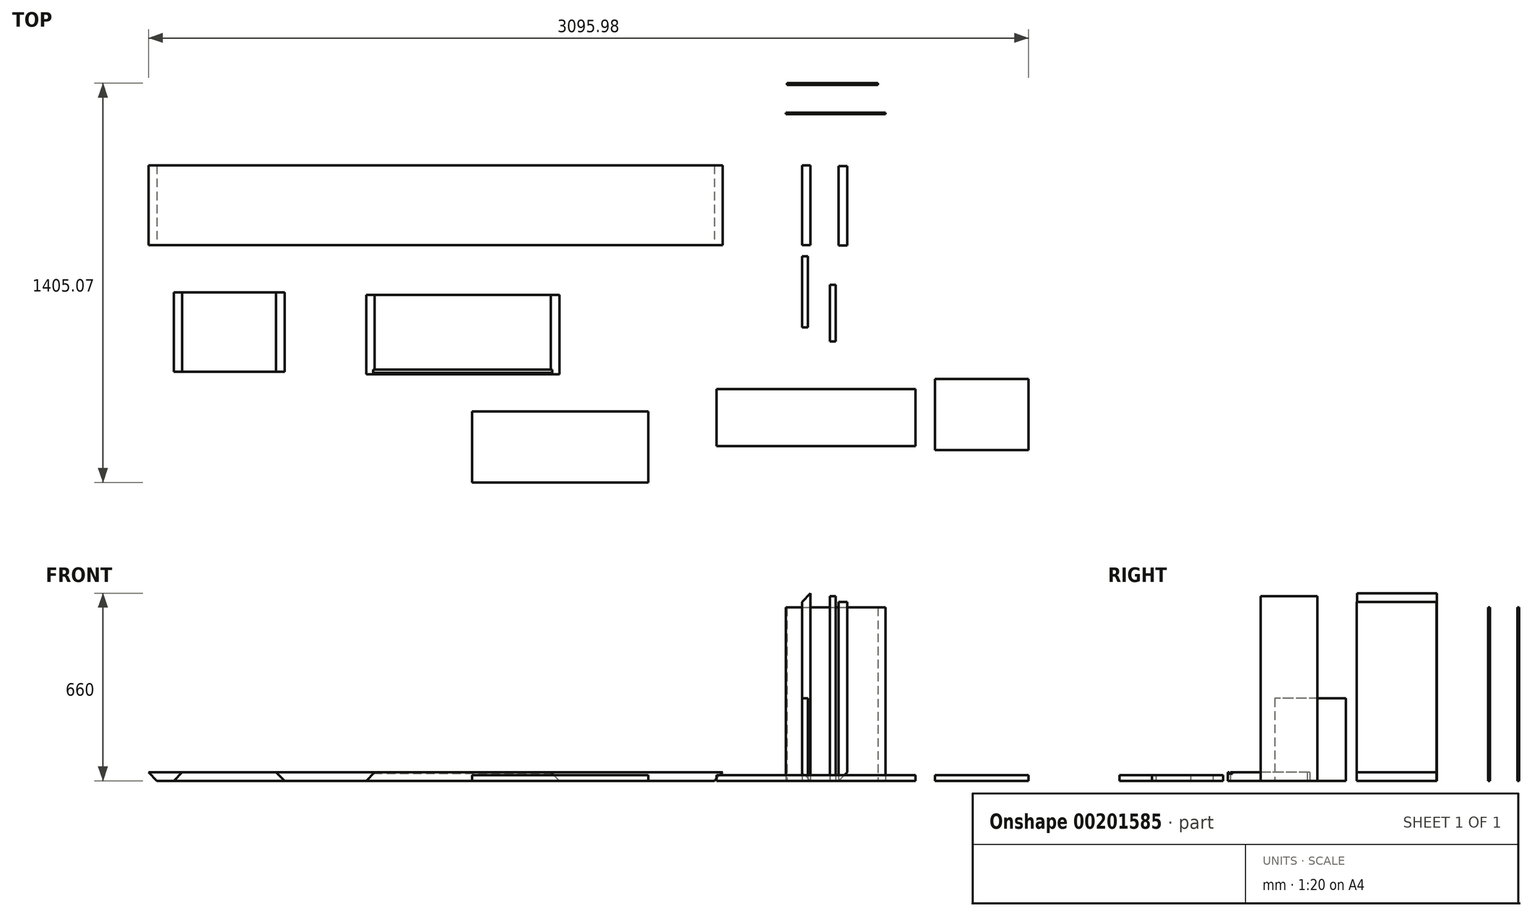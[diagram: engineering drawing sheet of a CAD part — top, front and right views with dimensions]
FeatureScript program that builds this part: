
annotation { "Feature Type Name" : "Feature", "Feature Type Description" : "" }
export const myFeature = defineFeature(function(context is Context, id is Id, definition is map)
    precondition{}
    {
        {
            var Q0;
            Q0=qCreatedBy(makeId("Top.planeOp"),FACE);
            var sketch = newSketch(context, id + "F0", { "sketchPlane" : qUnion([Q0])});
            skLineSegment(sketch, "E0.bottom", {"start": v(-100, 0) * mm, "end": v(-2120, 0) * mm});
            skLineSegment(sketch, "E0.top", {"start": v(-100, 280) * mm, "end": v(-2120, 280) * mm});
            skLineSegment(sketch, "E0.left", {"start": v(-100, 0) * mm, "end": v(-100, 280) * mm});
            skLineSegment(sketch, "E0.right", {"start": v(-2120, 0) * mm, "end": v(-2120, 280) * mm});
            skSolve(sketch);
        }
        {
            var Q0;
            Q0=makeQuery(id+"F0.imprint","IMPRINT",FACE,{"disambiguationData":[TD([[makeQuery(id+"F0.imprint","IMPRINT",EDGE,{"derivedFrom":sQuery(id+"F0.wireOp",EDGE,"E0.bottom")}),-1.0]])]});
            extrude(context, id + "F1", {"entities" : qUnion([Q0]), "depth" : 30 * mm});
        }
        {
            var Q0;
            Q0=qCreatedBy(makeId("Top.planeOp"),FACE);
            var sketch = newSketch(context, id + "F2", { "sketchPlane" : qUnion([Q0])});
            skLineSegment(sketch, "E1.bottom", {"start": v(178.97, 0) * mm, "end": v(208.97, 0) * mm});
            skLineSegment(sketch, "E1.top", {"start": v(178.97, 280) * mm, "end": v(208.97, 280) * mm});
            skLineSegment(sketch, "E1.left", {"start": v(178.97, 0) * mm, "end": v(178.97, 280) * mm});
            skLineSegment(sketch, "E1.right", {"start": v(208.97, 0) * mm, "end": v(208.97, 280) * mm});
            skSolve(sketch);
        }
        {
            var Q0;
            Q0=makeQuery(id+"F2.imprint","IMPRINT",FACE,{"disambiguationData":[TD([[makeQuery(id+"F2.imprint","IMPRINT",EDGE,{"derivedFrom":sQuery(id+"F2.wireOp",EDGE,"E1.bottom")}),1.0]])]});
            extrude(context, id + "F3", {"entities" : qUnion([Q0]), "depth" : 660 * mm});
        }
        {
            var Q0;
            Q0=makeQuery(id+"F1.opExtrude","SWEPT_FACE",FACE,{"disambiguationData":[OSD([sQuery(id+"F0.wireOp",EDGE,"E0.bottom")])]});
            var sketch = newSketch(context, id + "F4", { "sketchPlane" : qUnion([Q0])});
            skLineSegment(sketch, "E2", {"start": v(-100, 30) * mm, "end": v(-100, 0) * mm});
            skLineSegment(sketch, "E3", {"start": v(-100, 0) * mm, "end": v(-130, 0) * mm});
            skLineSegment(sketch, "E4", {"start": v(-130, 0) * mm, "end": v(-100, 30) * mm});
            skLineSegment(sketch, "E5", {"start": v(-2120, 30) * mm, "end": v(-2120, 0) * mm});
            skLineSegment(sketch, "E6", {"start": v(-2120, 0) * mm, "end": v(-2090, 0) * mm});
            skLineSegment(sketch, "E7", {"start": v(-2090, 0) * mm, "end": v(-2120, 30) * mm});
            skSolve(sketch);
        }
        {
            var Q0;
            Q0=makeQuery(id+"F4.imprint","IMPRINT",FACE,{"disambiguationData":[TD([[makeQuery(id+"F4.imprint","IMPRINT",EDGE,{"derivedFrom":sQuery(id+"F4.wireOp",EDGE,"E5")}),1.0]])]});
            var Q1;
            Q1=makeQuery(id+"F4.imprint","IMPRINT",FACE,{"disambiguationData":[TD([[makeQuery(id+"F4.imprint","IMPRINT",EDGE,{"derivedFrom":sQuery(id+"F4.wireOp",EDGE,"E2")}),-1.0]])]});
            extrude(context, id + "F5", {"entities" : qUnion([Q0, Q1]), "operationType" : NewBodyOperationType.REMOVE, "oppositeDirection" : true, "depth" : 380 * mm});
        }
        {
            var Q0;
            Q0=makeQuery(id+"F3.opExtrude","SWEPT_FACE",FACE,{"disambiguationData":[OSD([sQuery(id+"F2.wireOp",EDGE,"E1.bottom")])]});
            var sketch = newSketch(context, id + "F6", { "sketchPlane" : qUnion([Q0])});
            skLineSegment(sketch, "E8", {"start": v(208.97, 0) * mm, "end": v(178.97, 0) * mm});
            skLineSegment(sketch, "E9", {"start": v(178.97, 0) * mm, "end": v(178.97, 30) * mm});
            skLineSegment(sketch, "E10", {"start": v(178.97, 30) * mm, "end": v(208.97, 0) * mm});
            skLineSegment(sketch, "E11", {"start": v(208.97, 660) * mm, "end": v(178.97, 660) * mm});
            skLineSegment(sketch, "E12", {"start": v(178.97, 660) * mm, "end": v(178.97, 630) * mm});
            skLineSegment(sketch, "E13", {"start": v(178.97, 630) * mm, "end": v(208.97, 660) * mm});
            skSolve(sketch);
        }
        {
            var Q0;
            Q0=makeQuery(id+"F6.imprint","IMPRINT",FACE,{"disambiguationData":[TD([[makeQuery(id+"F6.imprint","IMPRINT",EDGE,{"derivedFrom":sQuery(id+"F6.wireOp",EDGE,"E11")}),-1.0]])]});
            var Q1;
            Q1=makeQuery(id+"F6.imprint","IMPRINT",FACE,{"disambiguationData":[TD([[makeQuery(id+"F6.imprint","IMPRINT",EDGE,{"derivedFrom":sQuery(id+"F6.wireOp",EDGE,"E8")}),1.0]])]});
            extrude(context, id + "F7", {"entities" : qUnion([Q0, Q1]), "operationType" : NewBodyOperationType.REMOVE, "oppositeDirection" : true, "depth" : 380 * mm});
        }
        {
            var Q0;
            Q0=qCreatedBy(makeId("Top.planeOp"),FACE);
            var sketch = newSketch(context, id + "F8", { "sketchPlane" : qUnion([Q0])});
            skLineSegment(sketch, "E14.bottom", {"start": v(-674.24, -175.08) * mm, "end": v(-1354.24, -175.08) * mm});
            skLineSegment(sketch, "E14.top", {"start": v(-674.24, -455.08) * mm, "end": v(-1354.24, -455.08) * mm});
            skLineSegment(sketch, "E14.left", {"start": v(-674.24, -175.08) * mm, "end": v(-674.24, -455.08) * mm});
            skLineSegment(sketch, "E14.right", {"start": v(-1354.24, -175.08) * mm, "end": v(-1354.24, -455.08) * mm});
            skSolve(sketch);
        }
        {
            var Q0;
            Q0=makeQuery(id+"F8.imprint","IMPRINT",FACE,{"disambiguationData":[TD([[makeQuery(id+"F8.imprint","IMPRINT",EDGE,{"derivedFrom":sQuery(id+"F8.wireOp",EDGE,"E14.bottom")}),1.0]])]});
            extrude(context, id + "F9", {"entities" : qUnion([Q0]), "depth" : 30 * mm});
        }
        {
            var Q0;
            Q0=qCreatedBy(makeId("Top.planeOp"),FACE);
            var sketch = newSketch(context, id + "F10", { "sketchPlane" : qUnion([Q0])});
            skLineSegment(sketch, "E15.bottom", {"start": v(179.68, -40) * mm, "end": v(199.68, -40) * mm});
            skLineSegment(sketch, "E15.top", {"start": v(179.68, -290) * mm, "end": v(199.68, -290) * mm});
            skLineSegment(sketch, "E15.left", {"start": v(179.68, -40) * mm, "end": v(179.68, -290) * mm});
            skLineSegment(sketch, "E15.right", {"start": v(199.68, -40) * mm, "end": v(199.68, -290) * mm});
            skSolve(sketch);
        }
        {
            var Q0;
            Q0=makeQuery(id+"F10.imprint","IMPRINT",FACE,{"disambiguationData":[TD([[makeQuery(id+"F10.imprint","IMPRINT",EDGE,{"derivedFrom":sQuery(id+"F10.wireOp",EDGE,"E15.bottom")}),-1.0]])]});
            extrude(context, id + "F11", {"entities" : qUnion([Q0]), "depth" : 290 * mm});
        }
        {
            var Q0;
            Q0=qCreatedBy(makeId("Top.planeOp"),FACE);
            var sketch = newSketch(context, id + "F12", { "sketchPlane" : qUnion([Q0])});
            skLineSegment(sketch, "E16.bottom", {"start": v(308, 278.64) * mm, "end": v(338, 278.64) * mm});
            skLineSegment(sketch, "E16.top", {"start": v(308, -1.36) * mm, "end": v(338, -1.36) * mm});
            skLineSegment(sketch, "E16.left", {"start": v(308, 278.64) * mm, "end": v(308, -1.36) * mm});
            skLineSegment(sketch, "E16.right", {"start": v(338, 278.64) * mm, "end": v(338, -1.36) * mm});
            skSolve(sketch);
        }
        {
            var Q0;
            Q0=makeQuery(id+"F12.imprint","IMPRINT",FACE,{"disambiguationData":[TD([[makeQuery(id+"F12.imprint","IMPRINT",EDGE,{"derivedFrom":sQuery(id+"F12.wireOp",EDGE,"E16.bottom")}),-1.0]])]});
            extrude(context, id + "F13", {"entities" : qUnion([Q0]), "depth" : 630 * mm});
        }
        {
            var Q0;
            Q0=makeQuery(id+"F13.opExtrude","SWEPT_FACE",FACE,{"disambiguationData":[OSD([sQuery(id+"F12.wireOp",EDGE,"E16.top")])]});
            var sketch = newSketch(context, id + "F14", { "sketchPlane" : qUnion([Q0])});
            skLineSegment(sketch, "E17", {"start": v(308, 0) * mm, "end": v(338, 0) * mm});
            skLineSegment(sketch, "E18", {"start": v(338, 0) * mm, "end": v(338, 30) * mm});
            skLineSegment(sketch, "E19", {"start": v(338, 30) * mm, "end": v(308, 0) * mm});
            skSolve(sketch);
        }
        {
            var Q0;
            Q0=makeQuery(id+"F14.imprint","IMPRINT",FACE,{"disambiguationData":[TD([[makeQuery(id+"F14.imprint","IMPRINT",EDGE,{"derivedFrom":sQuery(id+"F14.wireOp",EDGE,"E17")}),1.0]])]});
            extrude(context, id + "F15", {"entities" : qUnion([Q0]), "operationType" : NewBodyOperationType.REMOVE, "oppositeDirection" : true, "depth" : 380 * mm});
        }
        {
            var Q0;
            Q0=makeQuery(id+"F9.opExtrude","SWEPT_FACE",FACE,{"disambiguationData":[OSD([sQuery(id+"F8.wireOp",EDGE,"E14.top")])]});
            var sketch = newSketch(context, id + "F16", { "sketchPlane" : qUnion([Q0])});
            skLineSegment(sketch, "E20", {"start": v(-1354.24, 30) * mm, "end": v(-1324.24, 30) * mm});
            skLineSegment(sketch, "E21", {"start": v(-1324.24, 30) * mm, "end": v(-1354.24, 0) * mm});
            skLineSegment(sketch, "E22", {"start": v(-1354.24, 0) * mm, "end": v(-1354.24, 30) * mm});
            skLineSegment(sketch, "E23", {"start": v(-674.24, 30) * mm, "end": v(-704.24, 30) * mm});
            skLineSegment(sketch, "E24", {"start": v(-704.24, 30) * mm, "end": v(-674.24, 0) * mm});
            skLineSegment(sketch, "E25", {"start": v(-674.24, 0) * mm, "end": v(-674.24, 30) * mm});
            skSolve(sketch);
        }
        {
            var Q0;
            Q0 = qSketchRegion(id + "F16", true);
            extrude(context, id + "F17", {"entities" : qUnion([Q0]), "operationType" : NewBodyOperationType.REMOVE, "oppositeDirection" : true, "depth" : 380 * mm});
        }
        {
            var Q0;
            Q0=qCreatedBy(makeId("Top.planeOp"),FACE);
            var sketch = newSketch(context, id + "F18", { "sketchPlane" : qUnion([Q0])});
            skLineSegment(sketch, "E26.bottom", {"start": v(-1641.28, -166.12) * mm, "end": v(-2031.28, -166.12) * mm});
            skLineSegment(sketch, "E26.top", {"start": v(-1641.28, -446.12) * mm, "end": v(-2031.28, -446.12) * mm});
            skLineSegment(sketch, "E26.left", {"start": v(-1641.28, -166.12) * mm, "end": v(-1641.28, -446.12) * mm});
            skLineSegment(sketch, "E26.right", {"start": v(-2031.28, -166.12) * mm, "end": v(-2031.28, -446.12) * mm});
            skSolve(sketch);
        }
        {
            var Q0;
            Q0 = qSketchRegion(id + "F18", true);
            extrude(context, id + "F19", {"entities" : qUnion([Q0]), "depth" : 30 * mm});
        }
        {
            var Q0;
            Q0=makeQuery(id+"F19.opExtrude","SWEPT_FACE",FACE,{"disambiguationData":[OSD([sQuery(id+"F18.wireOp",EDGE,"E26.top")])]});
            var sketch = newSketch(context, id + "F20", { "sketchPlane" : qUnion([Q0])});
            skLineSegment(sketch, "E27", {"start": v(-2031.28, 0) * mm, "end": v(-2031.28, 30) * mm});
            skLineSegment(sketch, "E28", {"start": v(-2031.28, 30) * mm, "end": v(-2001.28, 30) * mm});
            skLineSegment(sketch, "E29", {"start": v(-2001.28, 30) * mm, "end": v(-2031.28, 0) * mm});
            skLineSegment(sketch, "E30", {"start": v(-1641.28, 0) * mm, "end": v(-1641.28, 30) * mm});
            skLineSegment(sketch, "E31", {"start": v(-1641.28, 30) * mm, "end": v(-1671.28, 30) * mm});
            skLineSegment(sketch, "E32", {"start": v(-1671.28, 30) * mm, "end": v(-1641.28, 0) * mm});
            skSolve(sketch);
        }
        {
            var Q0;
            Q0 = qSketchRegion(id + "F20", true);
            extrude(context, id + "F21", {"entities" : qUnion([Q0]), "operationType" : NewBodyOperationType.REMOVE, "oppositeDirection" : true, "depth" : 380 * mm});
        }
        {
            var Q0;
            Q0=makeQuery(id+"F9.opExtrude","CAP_FACE",FACE,{"disambiguationData":[OSD([sQuery(id+"F8.wireOp",EDGE,"E14.bottom"),sQuery(id+"F8.wireOp",EDGE,"E14.top"),sQuery(id+"F8.wireOp",EDGE,"E14.left"),sQuery(id+"F8.wireOp",EDGE,"E14.right")])],"isStart":false});
            var sketch = newSketch(context, id + "F22", { "sketchPlane" : qUnion([Q0])});
            skLineSegment(sketch, "E33.bottom", {"start": v(-674.24, -450.08) * mm, "end": v(-1434.24, -450.08) * mm});
            skLineSegment(sketch, "E33.top", {"start": v(-674.24, -438.08) * mm, "end": v(-1434.24, -438.08) * mm});
            skLineSegment(sketch, "E33.left", {"start": v(-674.24, -450.08) * mm, "end": v(-674.24, -438.08) * mm});
            skLineSegment(sketch, "E33.right", {"start": v(-1434.24, -450.08) * mm, "end": v(-1434.24, -438.08) * mm});
            skSolve(sketch);
        }
        {
            var Q0;
            Q0 = qSketchRegion(id + "F22", true);
            extrude(context, id + "F23", {"entities" : qUnion([Q0]), "operationType" : NewBodyOperationType.REMOVE, "oppositeDirection" : true, "depth" : 5 * mm});
        }
        {
            var Q0;
            Q0=qCreatedBy(makeId("Top.planeOp"),FACE);
            var sketch = newSketch(context, id + "F24", { "sketchPlane" : qUnion([Q0])});
            skLineSegment(sketch, "E34.bottom", {"start": v(122.05, 466.62) * mm, "end": v(472.05, 466.62) * mm});
            skLineSegment(sketch, "E34.top", {"start": v(122.05, 460.62) * mm, "end": v(472.05, 460.62) * mm});
            skLineSegment(sketch, "E34.left", {"start": v(122.05, 466.62) * mm, "end": v(122.05, 460.62) * mm});
            skLineSegment(sketch, "E34.right", {"start": v(472.05, 466.62) * mm, "end": v(472.05, 460.62) * mm});
            skSolve(sketch);
        }
        {
            var Q0;
            Q0 = qSketchRegion(id + "F24", true);
            extrude(context, id + "F25", {"entities" : qUnion([Q0]), "depth" : 610 * mm});
        }
        {
            var Q0;
            Q0=qCreatedBy(makeId("Top.planeOp"),FACE);
            var sketch = newSketch(context, id + "F26", { "sketchPlane" : qUnion([Q0])});
            skLineSegment(sketch, "E35.bottom", {"start": v(-361.56, -585.54) * mm, "end": v(-981.56, -585.54) * mm});
            skLineSegment(sketch, "E35.top", {"start": v(-361.56, -835.54) * mm, "end": v(-981.56, -835.54) * mm});
            skLineSegment(sketch, "E35.left", {"start": v(-361.56, -585.54) * mm, "end": v(-361.56, -835.54) * mm});
            skLineSegment(sketch, "E35.right", {"start": v(-981.56, -585.54) * mm, "end": v(-981.56, -835.54) * mm});
            skSolve(sketch);
        }
        {
            var Q0;
            Q0 = qSketchRegion(id + "F26", true);
            extrude(context, id + "F27", {"entities" : qUnion([Q0]), "depth" : 20 * mm});
        }
        {
            var Q0;
            Q0=qCreatedBy(makeId("Top.planeOp"),FACE);
            var sketch = newSketch(context, id + "F28", { "sketchPlane" : qUnion([Q0])});
            skLineSegment(sketch, "E36.bottom", {"start": v(277.47, -139.44) * mm, "end": v(297.47, -139.44) * mm});
            skLineSegment(sketch, "E36.top", {"start": v(277.47, -339.44) * mm, "end": v(297.47, -339.44) * mm});
            skLineSegment(sketch, "E36.left", {"start": v(277.47, -139.44) * mm, "end": v(277.47, -339.44) * mm});
            skLineSegment(sketch, "E36.right", {"start": v(297.47, -139.44) * mm, "end": v(297.47, -339.44) * mm});
            skSolve(sketch);
        }
        {
            var Q0;
            Q0 = qSketchRegion(id + "F28", true);
            extrude(context, id + "F29", {"entities" : qUnion([Q0]), "depth" : 650 * mm});
        }
        {
            var Q0;
            Q0=qCreatedBy(makeId("Top.planeOp"),FACE);
            var sketch = newSketch(context, id + "F30", { "sketchPlane" : qUnion([Q0])});
            skLineSegment(sketch, "E37.bottom", {"start": v(-122.18, -507.2) * mm, "end": v(577.82, -507.2) * mm});
            skLineSegment(sketch, "E37.top", {"start": v(-122.18, -707.2) * mm, "end": v(577.82, -707.2) * mm});
            skLineSegment(sketch, "E37.left", {"start": v(-122.18, -507.2) * mm, "end": v(-122.18, -707.2) * mm});
            skLineSegment(sketch, "E37.right", {"start": v(577.82, -507.2) * mm, "end": v(577.82, -707.2) * mm});
            skSolve(sketch);
        }
        {
            var Q0;
            Q0 = qSketchRegion(id + "F30", true);
            extrude(context, id + "F31", {"entities" : qUnion([Q0]), "depth" : 20 * mm});
        }
        {
            var Q0;
            Q0=qCreatedBy(makeId("Top.planeOp"),FACE);
            var sketch = newSketch(context, id + "F32", { "sketchPlane" : qUnion([Q0])});
            skLineSegment(sketch, "E38.bottom", {"start": v(645.98, -471.48) * mm, "end": v(975.98, -471.48) * mm});
            skLineSegment(sketch, "E38.top", {"start": v(645.98, -721.48) * mm, "end": v(975.98, -721.48) * mm});
            skLineSegment(sketch, "E38.left", {"start": v(645.98, -471.48) * mm, "end": v(645.98, -721.48) * mm});
            skLineSegment(sketch, "E38.right", {"start": v(975.98, -471.48) * mm, "end": v(975.98, -721.48) * mm});
            skSolve(sketch);
        }
        {
            var Q0;
            Q0=makeQuery(id+"F32.imprint","IMPRINT",FACE,{"disambiguationData":[TD([[makeQuery(id+"F32.imprint","IMPRINT",EDGE,{"derivedFrom":sQuery(id+"F32.wireOp",EDGE,"E38.bottom")}),-1.0]])]});
            extrude(context, id + "F33", {"entities" : qUnion([Q0]), "depth" : 20 * mm});
        }
        {
            var Q0;
            Q0=qCreatedBy(makeId("Top.planeOp"),FACE);
            var sketch = newSketch(context, id + "F34", { "sketchPlane" : qUnion([Q0])});
            skLineSegment(sketch, "E39.bottom", {"start": v(126.01, 563.53) * mm, "end": v(446.01, 563.53) * mm});
            skLineSegment(sketch, "E39.top", {"start": v(126.01, 569.53) * mm, "end": v(446.01, 569.53) * mm});
            skLineSegment(sketch, "E39.left", {"start": v(126.01, 563.53) * mm, "end": v(126.01, 569.53) * mm});
            skLineSegment(sketch, "E39.right", {"start": v(446.01, 563.53) * mm, "end": v(446.01, 569.53) * mm});
            skPoint(sketch, "E39.middle", {"position": v(286.01, 566.53) * mm});
            skSolve(sketch);
        }
        {
            var Q0;
            Q0 = qSketchRegion(id + "F34", true);
            extrude(context, id + "F35", {"entities" : qUnion([Q0]), "depth" : 610 * mm});
        }
    });
